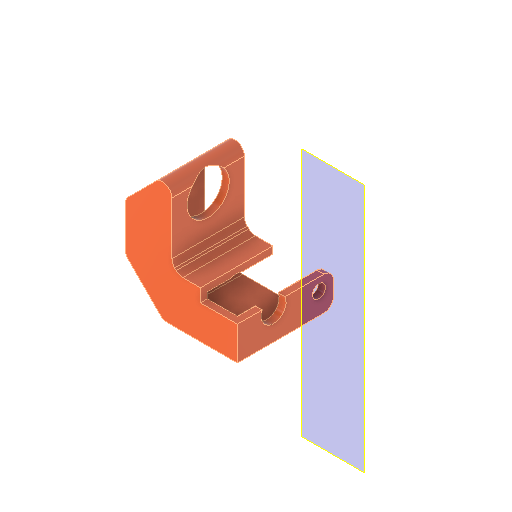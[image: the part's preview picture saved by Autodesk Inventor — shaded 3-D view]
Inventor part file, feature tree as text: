
AUTODESK INVENTOR PART (.ipt)
format: ipt  version: 2022 (Build 260153000, 153)  size: 278,528 bytes
history: native  units: in
note: dims shown in document units (in); Inventor stores cm internally (conversion verified against a paired STEP export)
features: other x8, extrude x7, sketch x6, reference x5, projected_geometry x2, plane x1, fillet x1
ambient origin geometry x8: Origin, YZ Plane, XZ Plane, XY Plane, X Axis, Y Axis, Z Axis, Center Point
bodies: Solid1 (feature_tree)
feature tree (30):
  plane  "Work Plane1"
  extrude  "Extrusion1"  Depth=0.5512in TaperAngle=0.0deg
  extrude  "Extrusion2"  Depth=0.0591in
  extrude  "Extrusion3"  TaperAngle=135.0deg  [1 undecoded]
  extrude  "Extrusion8"  Depth=0.2362in
  extrude  "Extrusion9"  Depth=0.2362in
  extrude  "Extrusion11"  Depth=0.5512in TaperAngle=0.0deg
  extrude  "Extrusion12"  Depth=0.0591in
  fillet  "Rundung1"  Radius=0.0591in
  sketch  "Sketch2"  dims[d0=0.0591in d1=0.0in d3=0.5512in d4=0.0in]
  sketch  "Sketch3"  dims[d12=0.0591in d13=0.0in d22=0.5307in]
  reference  "Reference1"
  projected_geometry  "Projected Loop5"
  projected_geometry  "Projected Loop6"
  sketch  "Sketch8"  dims[d23=0.2653in d25=135.0deg]
  reference  "Reference2"
  reference  "Reference3"
  sketch  "Sketch9"  dims[d26=0.1575in d27=0.2362in]
  reference  "Reference4"
  sketch  "Skizze11"  dims[d28=0.1568in d29=0.2362in]
  sketch  "Skizze12"  dims[d31=0.3937in d35=0.5512in d36=0.0in d40=0.0591in d41=0.0591in d42=0.9449in d43=0.5512in d44=0.0in d45=0.0in d48=0.0in d49=0.0in d50=0.1969in d51=0.3937in d52=0.0in d53=0.0787in]
  reference  "Referenz5"
  other  "<userpath>\Documents\Matchboxscope\INVENTOR\Matchboxscope_v0.iam"
  other  "Matchboxscope_v0.iam"
  other  "Matchboxscope_sample_v0:1"
  other  "Matchboxscope_middle2_v1:1"
  other  "00_ESP3-CAM:5"
  other  "Bauteil50"
  other  "Assembly_Matchboxscope_injectionmolded.iam"
  other  "IM_Matchboxscope_plate:2"
note: 1 required parameter value undecoded (feature->parameter linkage not recoverable at this tier; creation-order binding heuristic only, values carry confidence <= 0.55)
